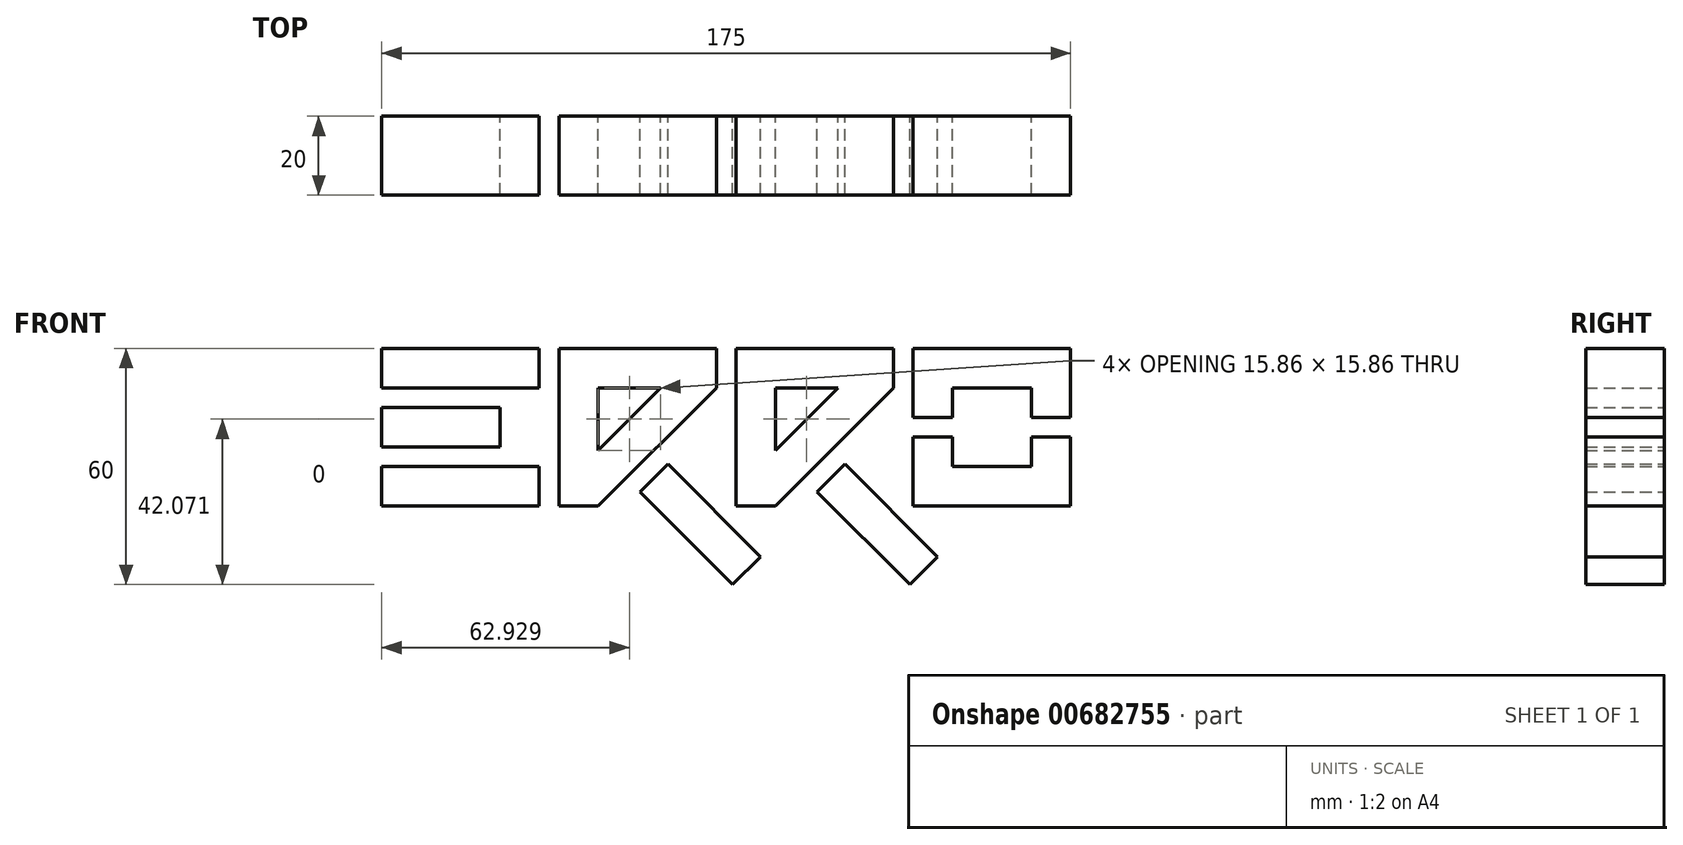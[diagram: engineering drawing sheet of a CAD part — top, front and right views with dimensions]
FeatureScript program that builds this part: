
annotation { "Feature Type Name" : "Feature", "Feature Type Description" : "" }
export const myFeature = defineFeature(function(context is Context, id is Id, definition is map)
    precondition{}
    {
        {
            var Q0;
            Q0=qCreatedBy(makeId("Front.planeOp"),FACE);
            var sketch = newSketch(context, id + "F0", { "sketchPlane" : qUnion([Q0])});
            skLineSegment(sketch, "E0.bottom", {"start": v(0, 0) * mm, "end": v(-40, 0) * mm});
            skLineSegment(sketch, "E0.top", {"start": v(0, 10) * mm, "end": v(-40, 10) * mm});
            skLineSegment(sketch, "E0.left", {"start": v(0, 0) * mm, "end": v(0, 10) * mm});
            skLineSegment(sketch, "E0.right", {"start": v(-40, 0) * mm, "end": v(-40, 10) * mm});
            skLineSegment(sketch, "E1.bottom", {"start": v(-40, 25) * mm, "end": v(-10, 25) * mm});
            skLineSegment(sketch, "E1.top", {"start": v(-40, 15) * mm, "end": v(-10, 15) * mm});
            skLineSegment(sketch, "E1.left", {"start": v(-40, 25) * mm, "end": v(-40, 15) * mm});
            skLineSegment(sketch, "E1.right", {"start": v(-10, 25) * mm, "end": v(-10, 15) * mm});
            skLineSegment(sketch, "E2.bottom", {"start": v(-40, 30) * mm, "end": v(0, 30) * mm});
            skLineSegment(sketch, "E2.top", {"start": v(-40, 40) * mm, "end": v(0, 40) * mm});
            skLineSegment(sketch, "E2.left", {"start": v(-40, 30) * mm, "end": v(-40, 40) * mm});
            skLineSegment(sketch, "E2.right", {"start": v(0, 30) * mm, "end": v(0, 40) * mm});
            skLineSegment(sketch, "E3", {"start": v(5, 0) * mm, "end": v(5, 40) * mm});
            skLineSegment(sketch, "E4", {"start": v(5, 40) * mm, "end": v(45, 40) * mm});
            skLineSegment(sketch, "E5", {"start": v(45, 40) * mm, "end": v(45, 30) * mm});
            skLineSegment(sketch, "E6", {"start": v(15, 0) * mm, "end": v(5, 0) * mm});
            skLineSegment(sketch, "E7", {"start": v(45, 30) * mm, "end": v(29.14, 14.14) * mm});
            skLineSegment(sketch, "E8", {"start": v(15, 0) * mm, "end": v(15, 0) * mm});
            skLineSegment(sketch, "E9", {"start": v(15, 30) * mm, "end": v(30.86, 30) * mm});
            skLineSegment(sketch, "E10", {"start": v(30.86, 30) * mm, "end": v(15, 14.14) * mm});
            skLineSegment(sketch, "E11", {"start": v(15, 14.14) * mm, "end": v(15, 30) * mm});
            skLineSegment(sketch, "E12", {"start": v(25.6, 3.54) * mm, "end": v(49.14, -20) * mm});
            skLineSegment(sketch, "E13", {"start": v(56.21, -12.93) * mm, "end": v(32.68, 10.6) * mm});
            skLineSegment(sketch, "E14", {"start": v(15, 14.14) * mm, "end": v(22.07, 7.07) * mm, "construction": true});
            skLineSegment(sketch, "E15.trimOffspring", {"start": v(22.07, 7.07) * mm, "end": v(15, 0) * mm});
            skLineSegment(sketch, "E16", {"start": v(50, 0) * mm, "end": v(50, 40) * mm});
            skLineSegment(sketch, "E17", {"start": v(50, 40) * mm, "end": v(90, 40) * mm});
            skLineSegment(sketch, "E18", {"start": v(90, 40) * mm, "end": v(90, 30) * mm});
            skLineSegment(sketch, "E19", {"start": v(60, 0) * mm, "end": v(50, 0) * mm});
            skLineSegment(sketch, "E20", {"start": v(90, 30) * mm, "end": v(74.14, 14.14) * mm});
            skLineSegment(sketch, "E21", {"start": v(60, 30) * mm, "end": v(75.86, 30) * mm});
            skLineSegment(sketch, "E22", {"start": v(75.86, 30) * mm, "end": v(60, 14.14) * mm});
            skLineSegment(sketch, "E23", {"start": v(60, 14.14) * mm, "end": v(60, 30) * mm});
            skLineSegment(sketch, "E24", {"start": v(70.6, 3.54) * mm, "end": v(94.14, -20) * mm});
            skLineSegment(sketch, "E25", {"start": v(101.21, -12.93) * mm, "end": v(77.68, 10.6) * mm});
            skLineSegment(sketch, "E26", {"start": v(60, 14.14) * mm, "end": v(67.07, 7.07) * mm, "construction": true});
            skLineSegment(sketch, "E27.trimOffspring", {"start": v(67.07, 7.07) * mm, "end": v(60, 0) * mm});
            skLineSegment(sketch, "E28.bottom", {"start": v(95, 0) * mm, "end": v(135, 0) * mm});
            skLineSegment(sketch, "E28.top", {"start": v(95, 40) * mm, "end": v(135, 40) * mm});
            skLineSegment(sketch, "E28.left", {"start": v(95, 0) * mm, "end": v(95, 17.5) * mm});
            skLineSegment(sketch, "E28.right", {"start": v(135, 0) * mm, "end": v(135, 17.5) * mm});
            skLineSegment(sketch, "E29.bottom", {"start": v(105, 30) * mm, "end": v(125, 30) * mm});
            skLineSegment(sketch, "E29.top", {"start": v(105, 10) * mm, "end": v(125, 10) * mm});
            skLineSegment(sketch, "E29.left", {"start": v(105, 30) * mm, "end": v(105, 22.5) * mm});
            skLineSegment(sketch, "E29.right", {"start": v(125, 30) * mm, "end": v(125, 22.5) * mm});
            skLineSegment(sketch, "E30", {"start": v(95, 17.5) * mm, "end": v(105, 17.5) * mm});
            skLineSegment(sketch, "E31", {"start": v(105, 22.5) * mm, "end": v(95, 22.5) * mm});
            skLineSegment(sketch, "E32", {"start": v(125, 22.5) * mm, "end": v(135, 22.5) * mm});
            skLineSegment(sketch, "E33", {"start": v(125, 17.5) * mm, "end": v(135, 17.5) * mm});
            skLineSegment(sketch, "E34.trimOffspring", {"start": v(95, 22.5) * mm, "end": v(95, 40) * mm});
            skLineSegment(sketch, "E35.trimOffspring", {"start": v(105, 17.5) * mm, "end": v(105, 10) * mm});
            skLineSegment(sketch, "E36.trimOffspring", {"start": v(125, 17.5) * mm, "end": v(125, 10) * mm});
            skLineSegment(sketch, "E37.trimOffspring", {"start": v(135, 22.5) * mm, "end": v(135, 40) * mm});
            skLineSegment(sketch, "E38", {"start": v(49.14, -20) * mm, "end": v(56.21, -12.93) * mm});
            skLineSegment(sketch, "E39", {"start": v(94.14, -20) * mm, "end": v(101.21, -12.93) * mm});
            skLineSegment(sketch, "E40", {"start": v(22.07, 7.07) * mm, "end": v(29.14, 14.14) * mm});
            skLineSegment(sketch, "E41", {"start": v(67.07, 7.07) * mm, "end": v(74.14, 14.14) * mm});
            skLineSegment(sketch, "E42", {"start": v(25.6, 3.54) * mm, "end": v(32.68, 10.6) * mm});
            skLineSegment(sketch, "E43", {"start": v(70.6, 3.54) * mm, "end": v(77.68, 10.6) * mm});
            skSolve(sketch);
        }
        {
            var Q0;
            Q0=makeQuery(id+"F0.imprint","IMPRINT",FACE,{"disambiguationData":[TD([[makeQuery(id+"F0.imprint","IMPRINT",EDGE,{"derivedFrom":sQuery(id+"F0.wireOp",EDGE,"E1.bottom")}),-1.0]])]});
            var Q1;
            Q1=makeQuery(id+"F0.imprint","IMPRINT",FACE,{"disambiguationData":[TD([[makeQuery(id+"F0.imprint","IMPRINT",EDGE,{"derivedFrom":sQuery(id+"F0.wireOp",EDGE,"E2.bottom")}),1.0]])]});
            var Q2;
            Q2=makeQuery(id+"F0.imprint","IMPRINT",FACE,{"disambiguationData":[TD([[makeQuery(id+"F0.imprint","IMPRINT",EDGE,{"derivedFrom":sQuery(id+"F0.wireOp",EDGE,"E0.bottom")}),-1.0]])]});
            var Q3;
            Q3=makeQuery(id+"F0.imprint","IMPRINT",FACE,{"disambiguationData":[TD([[makeQuery(id+"F0.imprint","IMPRINT",EDGE,{"derivedFrom":sQuery(id+"F0.wireOp",EDGE,"E3")}),-1.0]])]});
            var Q4;
            Q4=makeQuery(id+"F0.imprint","IMPRINT",FACE,{"disambiguationData":[TD([[makeQuery(id+"F0.imprint","IMPRINT",EDGE,{"derivedFrom":sQuery(id+"F0.wireOp",EDGE,"E12")}),1.0]])]});
            var Q5;
            Q5=makeQuery(id+"F0.imprint","IMPRINT",FACE,{"disambiguationData":[TD([[makeQuery(id+"F0.imprint","IMPRINT",EDGE,{"derivedFrom":sQuery(id+"F0.wireOp",EDGE,"E24")}),1.0]])]});
            var Q6;
            Q6=makeQuery(id+"F0.imprint","IMPRINT",FACE,{"disambiguationData":[TD([[makeQuery(id+"F0.imprint","IMPRINT",EDGE,{"derivedFrom":sQuery(id+"F0.wireOp",EDGE,"E16")}),-1.0]])]});
            var Q7;
            Q7=makeQuery(id+"F0.imprint","IMPRINT",FACE,{"disambiguationData":[TD([[makeQuery(id+"F0.imprint","IMPRINT",EDGE,{"derivedFrom":sQuery(id+"F0.wireOp",EDGE,"E28.top")}),-1.0]])]});
            var Q8;
            Q8=makeQuery(id+"F0.imprint","IMPRINT",FACE,{"disambiguationData":[TD([[makeQuery(id+"F0.imprint","IMPRINT",EDGE,{"derivedFrom":sQuery(id+"F0.wireOp",EDGE,"E28.bottom")}),1.0]])]});
            extrude(context, id + "F1", {"entities" : qUnion([Q0, Q1, Q2, Q3, Q4, Q5, Q6, Q7, Q8]), "depth" : 20 * mm, "offsetDistance" : 25 * mm});
        }
    });
